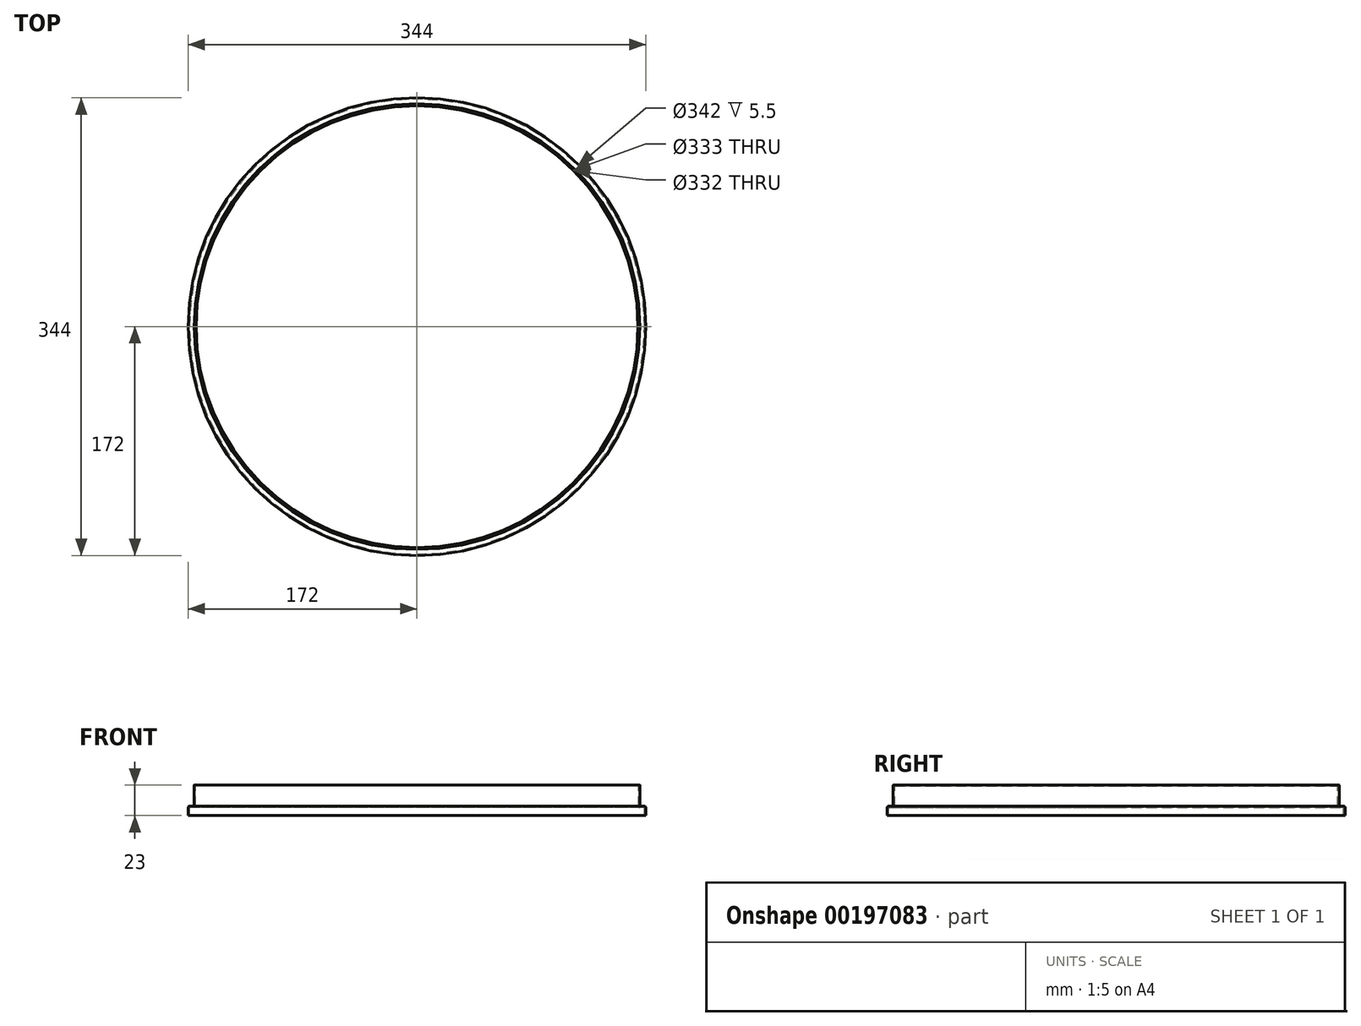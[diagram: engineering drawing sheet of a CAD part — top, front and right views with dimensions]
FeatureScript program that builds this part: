
annotation { "Feature Type Name" : "Feature", "Feature Type Description" : "" }
export const myFeature = defineFeature(function(context is Context, id is Id, definition is map)
    precondition{}
    {
        {
            var Q0;
            Q0=qCreatedBy(makeId("Front.planeOp"),FACE);
            var sketch = newSketch(context, id + "F0", { "sketchPlane" : qUnion([Q0])});
            skLineSegment(sketch, "E0", {"start": v(-166.5, 16.4) * mm, "end": v(-166.5, 1) * mm});
            skLineSegment(sketch, "E1", {"start": v(-167.5, 0) * mm, "end": v(-170.5, 0) * mm});
            skLineSegment(sketch, "E2", {"start": v(-171, -0.5) * mm, "end": v(-171, -6) * mm});
            skLineSegment(sketch, "E3", {"start": v(-171, -6) * mm, "end": v(-172, -6) * mm});
            skLineSegment(sketch, "E4", {"start": v(-172, -6) * mm, "end": v(-172, 0) * mm});
            skLineSegment(sketch, "E5", {"start": v(-171, 1) * mm, "end": v(-168, 1) * mm});
            skLineSegment(sketch, "E6", {"start": v(-167.5, 1.5) * mm, "end": v(-167.5, 16.8) * mm});
            skLineSegment(sketch, "E7", {"start": v(-167.3, 17) * mm, "end": v(-166.7, 17) * mm});
            skPoint(sketch, "E8.visualSharp", {"position": v(-172, 1) * mm});
            skArc(sketch, "E8.filletArc", {"start": v(-171, 1) * mm, "mid": v(-171.7, 0.7) * mm, "end": v(-172, 0) * mm});
            skArc(sketch, "E9.filletArc", {"start": v(-170.5, 0) * mm, "mid": v(-170.85, -0.15) * mm, "end": v(-171, -0.5) * mm});
            skPoint(sketch, "E10.visualSharp", {"position": v(-166.5, 0) * mm});
            skArc(sketch, "E10.filletArc", {"start": v(-167.5, 0) * mm, "mid": v(-166.8, 0.3) * mm, "end": v(-166.5, 1) * mm});
            skArc(sketch, "E11.filletArc", {"start": v(-168, 1) * mm, "mid": v(-167.65, 1.15) * mm, "end": v(-167.5, 1.5) * mm});
            skPoint(sketch, "E12.visualSharp", {"position": v(-166.5, 17) * mm});
            skPoint(sketch, "E13.visualSharp", {"position": v(-167.5, 17) * mm});
            skArc(sketch, "E13.filletArc", {"start": v(-167.3, 17) * mm, "mid": v(-167.44, 16.94) * mm, "end": v(-167.5, 16.8) * mm});
            skLineSegment(sketch, "E14", {"start": v(0, 38.91) * mm, "end": v(0, -32.55) * mm, "construction": true});
            skLineSegment(sketch, "E15", {"start": v(-167.5, 17) * mm, "end": v(-166.1, 17) * mm});
            skLineSegment(sketch, "E16", {"start": v(-166, 16.9) * mm, "end": v(-166, 16.6) * mm});
            skLineSegment(sketch, "E17", {"start": v(-166.1, 16.5) * mm, "end": v(-166.4, 16.5) * mm});
            skPoint(sketch, "E18.visualSharp", {"position": v(-166, 17) * mm});
            skArc(sketch, "E18.filletArc", {"start": v(-166, 16.9) * mm, "mid": v(-166.03, 16.97) * mm, "end": v(-166.1, 17) * mm});
            skPoint(sketch, "E19.visualSharp", {"position": v(-166, 16.5) * mm});
            skArc(sketch, "E19.filletArc", {"start": v(-166.1, 16.5) * mm, "mid": v(-166.03, 16.53) * mm, "end": v(-166, 16.6) * mm});
            skPoint(sketch, "E20.visualSharp", {"position": v(-166.5, 16.5) * mm});
            skArc(sketch, "E20.filletArc", {"start": v(-166.4, 16.5) * mm, "mid": v(-166.47, 16.47) * mm, "end": v(-166.5, 16.4) * mm});
            skSolve(sketch);
        }
        {
            var Q0;
            Q0=makeQuery(id+"F0.imprint","IMPRINT",FACE,{"disambiguationData":[TD([[makeQuery(id+"F0.imprint","IMPRINT",EDGE,{"derivedFrom":sQuery(id+"F0.wireOp",EDGE,"E0")}),-1.0]])]});
            var Q1;
            Q1=sQuery(id+"F0.wireOp",EDGE,"E14");
            revolve(context, id + "F1", {"entities" : qUnion([Q0]), "axis" : qUnion([Q1]), "revolveType" : RevolveType.FULL});
        }
    });
